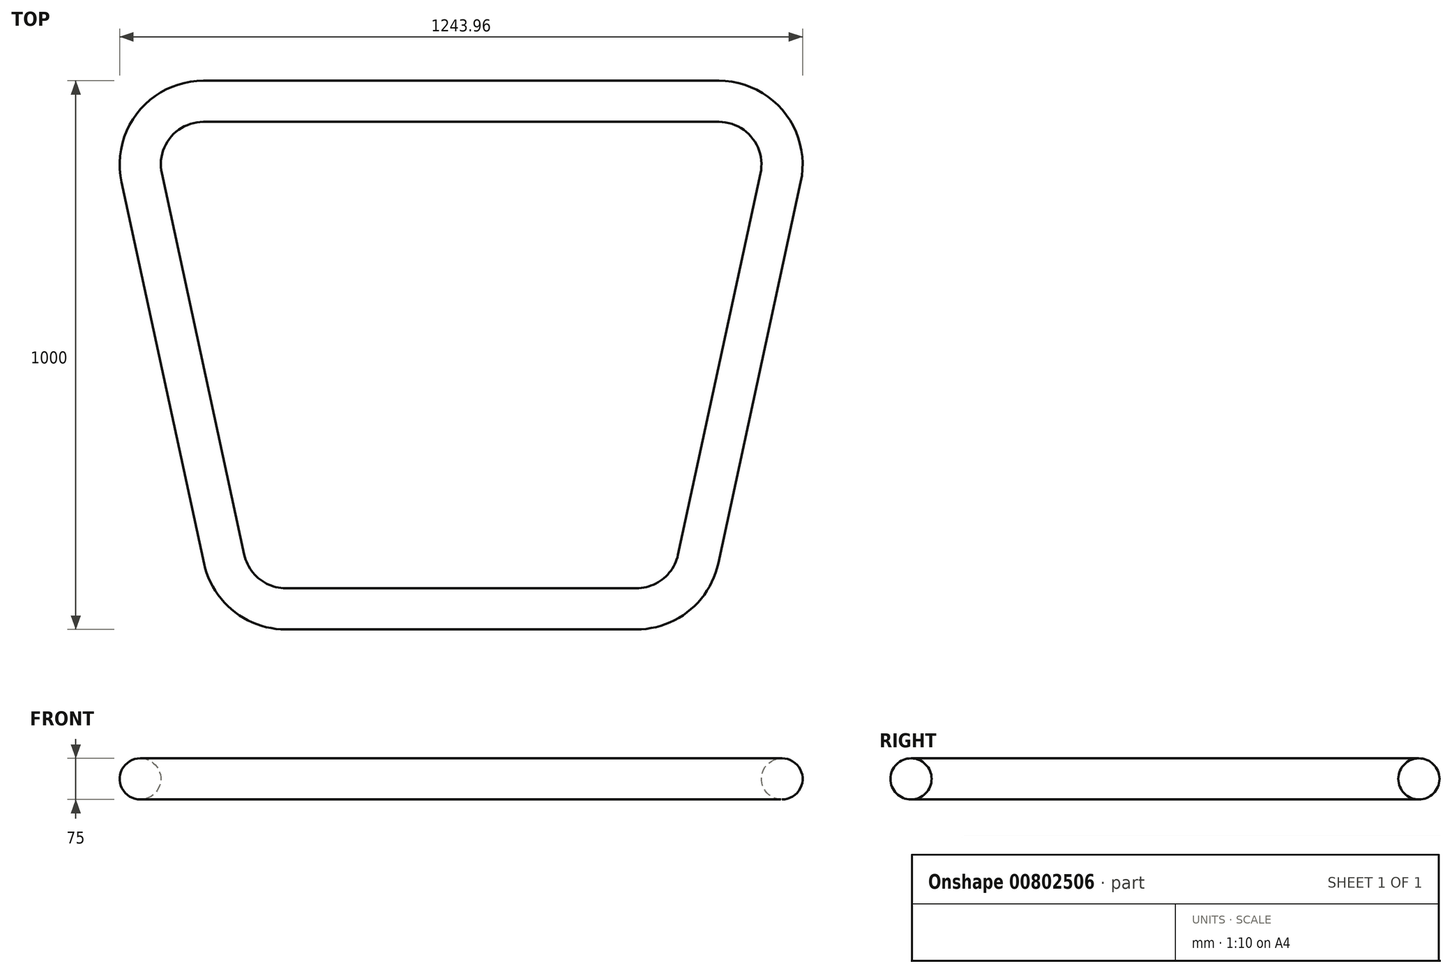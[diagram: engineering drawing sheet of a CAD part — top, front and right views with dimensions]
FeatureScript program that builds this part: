
annotation { "Feature Type Name" : "Feature", "Feature Type Description" : "" }
export const myFeature = defineFeature(function(context is Context, id is Id, definition is map)
    precondition{}
    {
        {
            var Q0;
            Q0=qCreatedBy(makeId("Top.planeOp"),FACE);
            var sketch = newSketch(context, id + "F0", { "sketchPlane" : qUnion([Q0])});
            skLineSegment(sketch, "E0", {"start": v(-469.48, 462.5) * mm, "end": v(469.48, 462.5) * mm});
            skLineSegment(sketch, "E1", {"start": v(581.88, 323.2) * mm, "end": v(431.61, -371.8) * mm});
            skLineSegment(sketch, "E2", {"start": v(319.2, -462.5) * mm, "end": v(-319.2, -462.5) * mm});
            skLineSegment(sketch, "E3", {"start": v(-431.61, -371.8) * mm, "end": v(-581.88, 323.2) * mm});
            skPoint(sketch, "E4.visualSharp", {"position": v(612, 462.5) * mm});
            skArc(sketch, "E4.filletArc", {"start": v(581.88, 323.2) * mm, "mid": v(558.98, 419.72) * mm, "end": v(469.48, 462.5) * mm});
            skPoint(sketch, "E5.visualSharp", {"position": v(412, -462.5) * mm});
            skArc(sketch, "E5.filletArc", {"start": v(319.2, -462.5) * mm, "mid": v(391.42, -437) * mm, "end": v(431.61, -371.8) * mm});
            skPoint(sketch, "E6.visualSharp", {"position": v(-412, -462.5) * mm});
            skArc(sketch, "E6.filletArc", {"start": v(-431.61, -371.8) * mm, "mid": v(-391.42, -437) * mm, "end": v(-319.2, -462.5) * mm});
            skPoint(sketch, "E7.visualSharp", {"position": v(-612, 462.5) * mm});
            skArc(sketch, "E7.filletArc", {"start": v(-469.48, 462.5) * mm, "mid": v(-558.98, 419.72) * mm, "end": v(-581.88, 323.2) * mm});
            skSolve(sketch);
        }
        {
            var Q0;
            Q0=qCreatedBy(makeId("Right.planeOp"),FACE);
            var sketch = newSketch(context, id + "F1", { "sketchPlane" : qUnion([Q0])});
            skCircle(sketch, "E8", {"center": v(462.5, 0) * mm, "radius": 37.5 * mm});
            skSolve(sketch);
        }
        {
            var Q0;
            Q0=makeQuery(id+"F1.imprint","IMPRINT",FACE,{"disambiguationData":[TD([[makeQuery(id+"F1.imprint","IMPRINT",EDGE,{"derivedFrom":sQuery(id+"F1.wireOp",EDGE,"E8")}),1.0]])]});
            var Q1;
            Q1=sQuery(id+"F0.wireOp",EDGE,"E0");
            var Q2;
            Q2=sQuery(id+"F0.wireOp",EDGE,"E4.filletArc");
            var Q3;
            Q3=sQuery(id+"F0.wireOp",EDGE,"E1");
            var Q4;
            Q4=sQuery(id+"F0.wireOp",EDGE,"E5.filletArc");
            var Q5;
            Q5=sQuery(id+"F0.wireOp",EDGE,"E2");
            var Q6;
            Q6=sQuery(id+"F0.wireOp",EDGE,"E6.filletArc");
            var Q7;
            Q7=sQuery(id+"F0.wireOp",EDGE,"E3");
            var Q8;
            Q8=sQuery(id+"F0.wireOp",EDGE,"E7.filletArc");
            sweep(context, id + "F2", {"profiles" : qUnion([Q0]), "path" : qUnion([Q1, Q2, Q3, Q4, Q5, Q6, Q7, Q8])});
        }
    });
